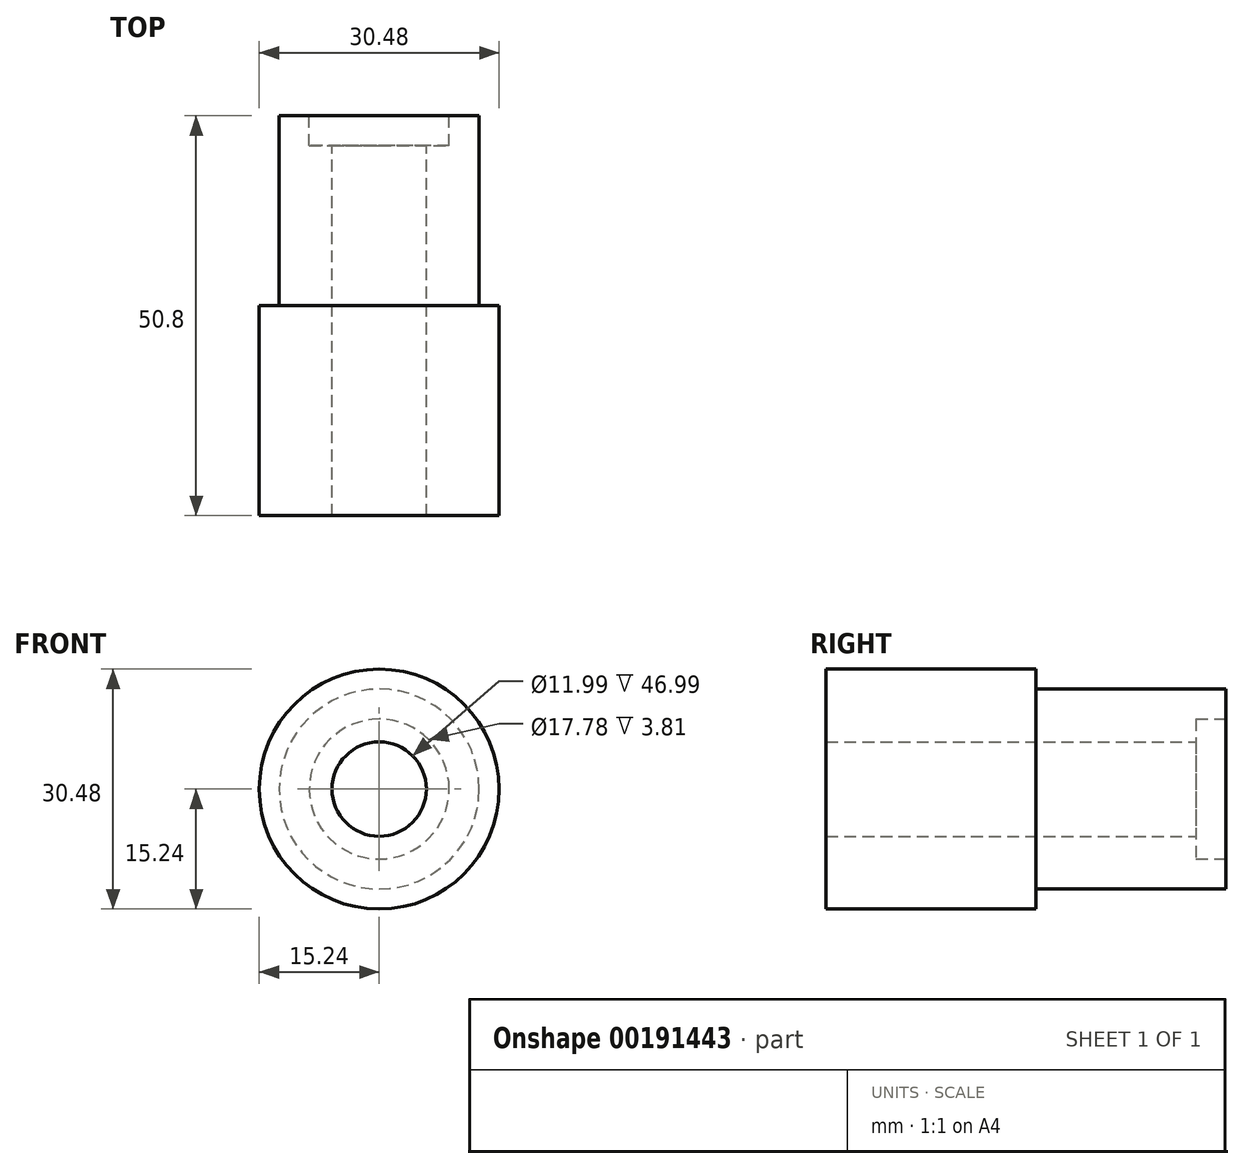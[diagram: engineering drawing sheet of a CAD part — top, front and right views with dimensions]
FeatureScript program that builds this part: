
annotation { "Feature Type Name" : "Feature", "Feature Type Description" : "" }
export const myFeature = defineFeature(function(context is Context, id is Id, definition is map)
    precondition{}
    {
        {
            var Q0;
            Q0=qCreatedBy(makeId("Front.planeOp"),FACE);
            var sketch = newSketch(context, id + "F0", { "sketchPlane" : qUnion([Q0])});
            skCircle(sketch, "E0", {"center": v(0, 0) * mm, "radius": 15.24 * mm});
            skCircle(sketch, "E1", {"center": v(0, 0) * mm, "radius": 6 * mm});
            skSolve(sketch);
        }
        {
            var Q0;
            Q0 = qSketchRegion(id + "F0", true);
            extrude(context, id + "F1", {"entities" : qUnion([Q0]), "depth" : 50.8 * mm});
        }
        {
            var Q0;
            Q0=makeQuery(id+"F1.opExtrude","CAP_FACE",FACE,{"disambiguationData":[OSD([sQuery(id+"F0.wireOp",EDGE,"E0"),sQuery(id+"F0.wireOp",EDGE,"E1")])],"isStart":true});
            var sketch = newSketch(context, id + "F2", { "sketchPlane" : qUnion([Q0])});
            skCircle(sketch, "E2", {"center": v(0, 0) * mm, "radius": 12.7 * mm});
            skCircle(sketch, "E3", {"center": v(0, 0) * mm, "radius": 18.44 * mm});
            skSolve(sketch);
        }
        {
            var Q0;
            Q0 = qSketchRegion(id + "F2", true);
            extrude(context, id + "F3", {"entities" : qUnion([Q0]), "operationType" : NewBodyOperationType.REMOVE, "oppositeDirection" : true, "depth" : 24.13 * mm});
        }
        {
            var Q0;
            Q0=makeQuery(id+"F1.opExtrude","CAP_FACE",FACE,{"disambiguationData":[OSD([sQuery(id+"F0.wireOp",EDGE,"E0"),sQuery(id+"F0.wireOp",EDGE,"E1")])],"isStart":true});
            var sketch = newSketch(context, id + "F4", { "sketchPlane" : qUnion([Q0])});
            skCircle(sketch, "E4", {"center": v(0, 0) * mm, "radius": 8.9 * mm});
            skSolve(sketch);
        }
        {
            var Q0;
            Q0 = qSketchRegion(id + "F4", true);
            extrude(context, id + "F5", {"entities" : qUnion([Q0]), "operationType" : NewBodyOperationType.REMOVE, "oppositeDirection" : true, "depth" : 3.8 * mm});
        }
    });
